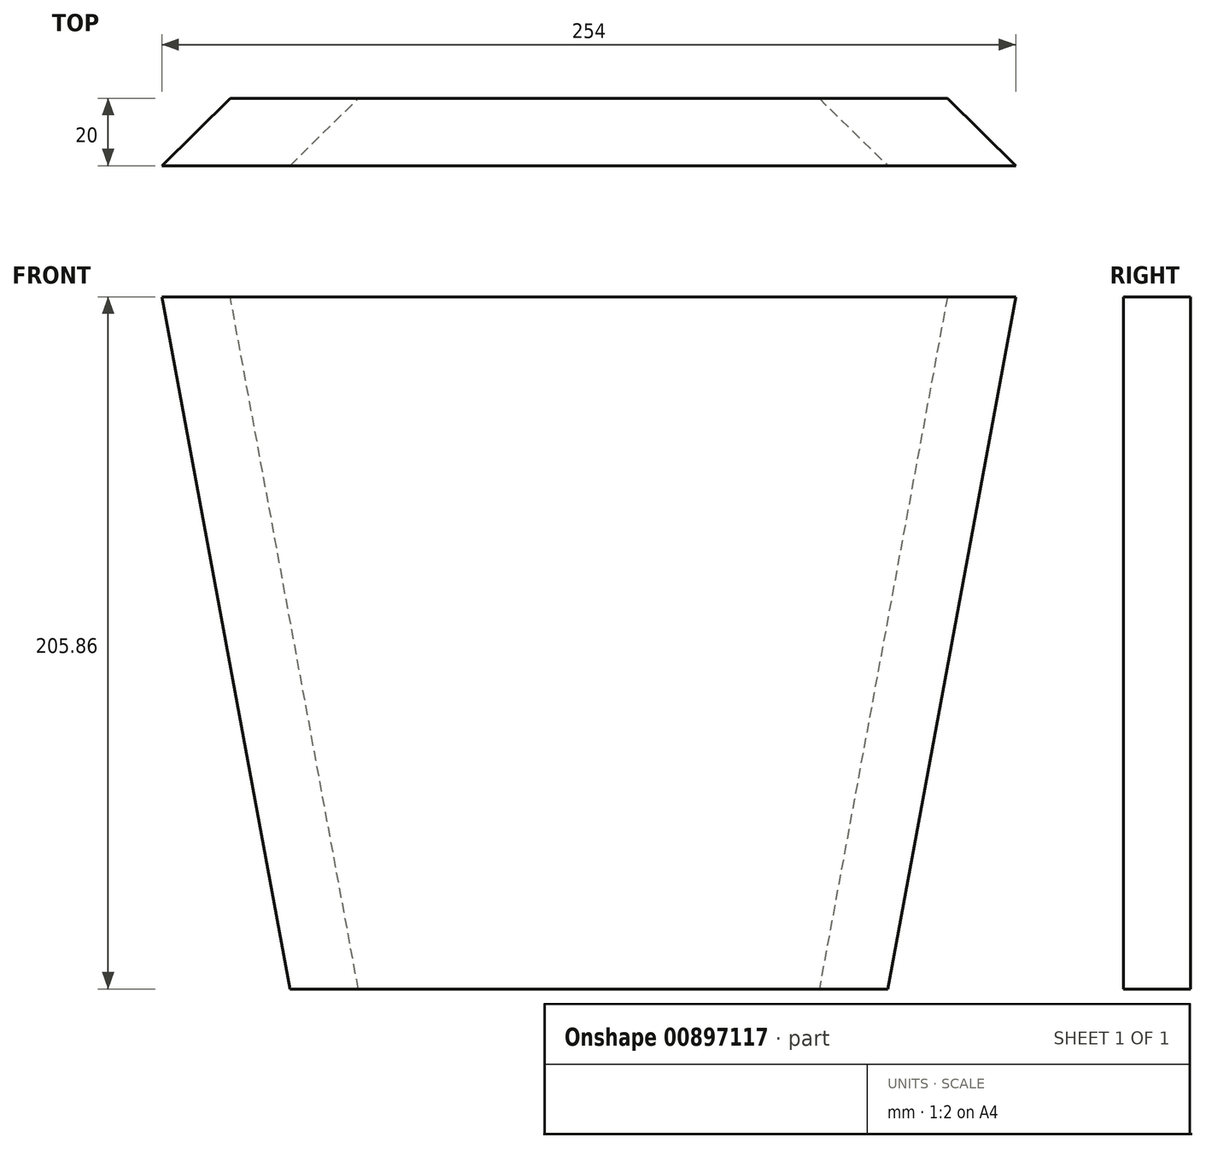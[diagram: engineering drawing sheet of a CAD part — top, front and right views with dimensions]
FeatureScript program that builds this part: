
annotation { "Feature Type Name" : "Feature", "Feature Type Description" : "" }
export const myFeature = defineFeature(function(context is Context, id is Id, definition is map)
    precondition{}
    {
        {
            var Q0;
            Q0=qCreatedBy(makeId("Front.planeOp"),FACE);
            var sketch = newSketch(context, id + "F0", { "sketchPlane" : qUnion([Q0])});
            skLineSegment(sketch, "E0", {"start": v(71.51, -110.87) * mm, "end": v(-106.29, -110.87) * mm});
            skLineSegment(sketch, "E1", {"start": v(-106.29, -110.87) * mm, "end": v(-144.39, 94.99) * mm});
            skLineSegment(sketch, "E2", {"start": v(-144.39, 94.99) * mm, "end": v(109.61, 94.99) * mm});
            skLineSegment(sketch, "E3", {"start": v(109.61, 94.99) * mm, "end": v(71.51, -110.87) * mm});
            skLineSegment(sketch, "E4", {"start": v(-144.39, 94.99) * mm, "end": v(-144.39, -110.87) * mm});
            skLineSegment(sketch, "E5", {"start": v(-144.39, -110.87) * mm, "end": v(-106.29, -110.87) * mm});
            skLineSegment(sketch, "E6", {"start": v(109.61, 94.99) * mm, "end": v(109.61, -110.87) * mm});
            skLineSegment(sketch, "E7", {"start": v(109.61, -110.87) * mm, "end": v(71.51, -110.87) * mm});
            skSolve(sketch);
        }
        {
            var Q0;
            Q0=makeQuery(id+"F0.imprint","IMPRINT",FACE,{"disambiguationData":[TD([[makeQuery(id+"F0.imprint","IMPRINT",EDGE,{"derivedFrom":sQuery(id+"F0.wireOp",EDGE,"E0")}),-1.0]])]});
            extrude(context, id + "F1", {"entities" : qUnion([Q0]), "depth" : 20 * mm, "offsetDistance" : 25.4 * mm});
        }
        {
            var Q0;
            Q0=makeQuery(id+"F1.opExtrude","CAP_EDGE",EDGE,{"disambiguationData":[OSD([sQuery(id+"F0.wireOp",EDGE,"E3")])],"isStart":true});
            chamfer(context, id + "F2", {"entities" : qUnion([Q0]), "width" : 20 * mm, "tangentPropagation" : true});
        }
        {
            var Q0;
            Q0=makeQuery(id+"F1.opExtrude","CAP_EDGE",EDGE,{"disambiguationData":[OSD([sQuery(id+"F0.wireOp",EDGE,"E1")])],"isStart":true});
            chamfer(context, id + "F3", {"entities" : qUnion([Q0]), "width" : 20 * mm, "tangentPropagation" : true});
        }
    });
